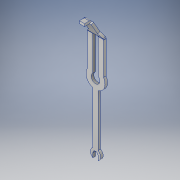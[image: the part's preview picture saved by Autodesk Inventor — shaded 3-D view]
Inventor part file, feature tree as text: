
AUTODESK INVENTOR PART (.ipt)
format: ipt  version: 2018 (Build 220112000, 112)  size: 182,784 bytes
history: native  units: in
note: dims shown in document units (in); Inventor stores cm internally (conversion verified against a paired STEP export)
features: sketch x3, other x2, extrude x1, plane x1
ambient origin geometry x8: Origin, YZ Plane, XZ Plane, XY Plane, X Axis, Y Axis, Z Axis, Center Point
bodies: Solid1 (feature_tree)
feature tree (7):
  extrude  "Extrusion1"  Depth=0.159in
  other  "Bend Part1"
  plane  "Work Plane1"
  other  "Bend Part2"
  sketch  "Sketch1"  dims[d0=0.08in d1=0.159in]
  sketch  "Sketch2"  dims[d3=0.8in]
  sketch  "Sketch3"  dims[d5=0.08in d6=0.135in d8=0.25in d9=0.5in d10=0.085in d11=0.14in d12=0.2in d13=0.08in d14=0.08in d15=0.04in d16=0.0in d17=0.05in d18=30.0deg d19=0.0in d20=0.0in d21=60.0deg]
